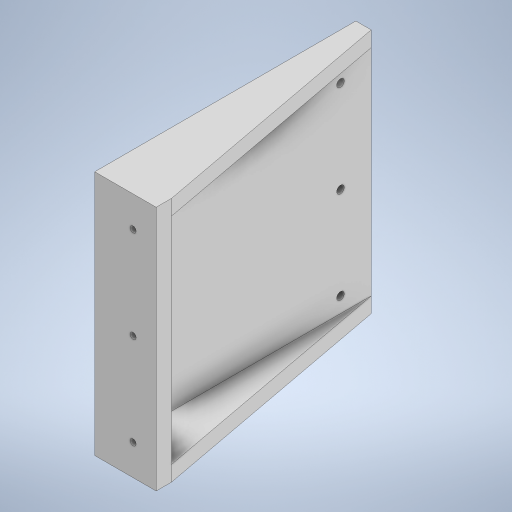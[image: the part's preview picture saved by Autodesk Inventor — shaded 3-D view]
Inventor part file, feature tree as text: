
AUTODESK INVENTOR PART (.ipt)
format: ipt  version: 2023 (Build 270158000, 158)  size: 314,368 bytes
history: native  units: mm
features: extrude x7, sketch x7
ambient origin geometry x8: Origin, YZ Plane, XZ Plane, XY Plane, X Axis, Y Axis, Z Axis, Center Point
bodies: Body1 (feature_tree)
feature tree (14):
  extrude  "Extrusion15"  Depth=160.0mm
  extrude  "Extrusion16"  Depth=170.0mm
  extrude  "Extrusion17"  Depth=10.0mm TaperAngle=0.0deg
  extrude  "Extrusion18"  Depth=10.0mm TaperAngle=0.0deg
  extrude  "Extrusion19"  Depth=4.0mm
  extrude  "Extrusion20"  Depth=4.0mm TaperAngle=0.0deg
  extrude  "Extrusion21"  Depth=4.0mm
  sketch  "Sketch21"  dims[d53=30.0mm d1=160.0mm]
  sketch  "Sketch22"  dims[d55=10.0mm d56=0.0mm d57=170.0mm]
  sketch  "Sketch23"  dims[d58=160.0mm d59=10.0mm d60=0.0mm]
  sketch  "Sketch24"  dims[d61=10.0mm d62=0.0mm d63=10.0mm d64=0.0mm]
  sketch  "Sketch25"  dims[d65=4.0mm d66=4.0mm]
  sketch  "Sketch27"  dims[d67=4.0mm d68=20.0mm d69=0.0mm]
  sketch  "Sketch29"  dims[d70=20.0mm d71=20.0mm d72=80.0mm d73=20.0mm d74=5.0mm d75=5.0mm d76=80.0mm d77=5.0mm d78=20.0mm d79=20.0mm d80=20.0mm d81=20.0mm d82=20.0mm d83=0.0mm d84=5.0mm d85=20.0mm d86=80.0mm d87=5.0mm d88=20.0mm d89=20.0mm d90=5.0mm d91=20.0mm d92=20.0mm d93=10.0mm d94=10.0mm d95=10.0mm d96=10.0mm d97=10.0mm d98=10.0mm d99=4.0mm d100=0.0mm d49=0.5mm d50=0.872665mm d51=0.5mm d52=0.872665mm]
